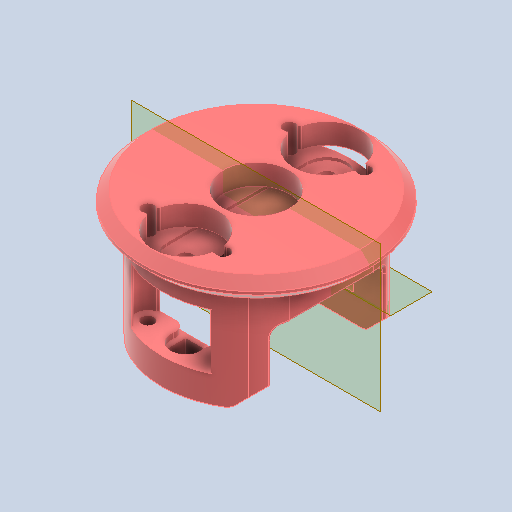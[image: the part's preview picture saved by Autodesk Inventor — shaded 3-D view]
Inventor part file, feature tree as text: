
AUTODESK INVENTOR PART (.ipt)
format: ipt  version: 2022 (Build 260153000, 153)  size: 475,648 bytes
history: native  units: in
note: dims shown in document units (in); Inventor stores cm internally (conversion verified against a paired STEP export)
features: sketch x13, other x3
ambient origin geometry x8: Origin, YZ Plane, XZ Plane, XY Plane, X Axis, Y Axis, Z Axis, Center Point
bodies: Solid1 (feature_tree)
feature tree (16):
  other  "Undercarriage_MIR.ipt"
  other  "Solid1::Undercarriage_MIR.ipt"
  other  "TaggingFeature1"
  sketch  "Sketch1"  dims[d0=0.3937in]
  sketch  "Sketch2"
  sketch  "Sketch9"
  sketch  "Sketch6"
  sketch  "Sketch7"
  sketch  "Sketch8"
  sketch  "Sketch10"
  sketch  "Sketch11"
  sketch  "Sketch12"
  sketch  "Sketch13"
  sketch  "Sketch14"
  sketch  "Sketch15"
  sketch  "Sketch16"
